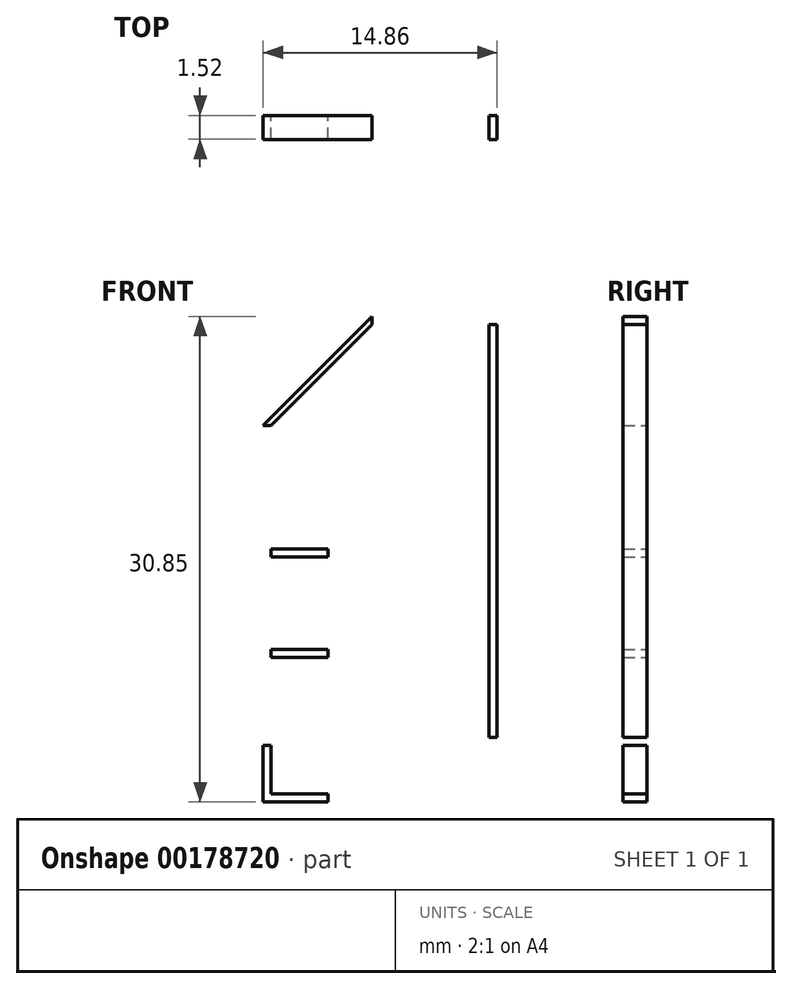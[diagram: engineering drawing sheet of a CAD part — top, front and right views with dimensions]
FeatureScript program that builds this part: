
annotation { "Feature Type Name" : "Feature", "Feature Type Description" : "" }
export const myFeature = defineFeature(function(context is Context, id is Id, definition is map)
    precondition{}
    {
        {
            var Q0;
            Q0=qCreatedBy(makeId("Front.planeOp"),FACE);
            var sketch = newSketch(context, id + "F0", { "sketchPlane" : qUnion([Q0])});
            skLineSegment(sketch, "E0", {"start": v(9.23, -10.4) * mm, "end": v(9.23, 27.78) * mm, "construction": true});
            skLineSegment(sketch, "E1", {"start": v(9.23, -10.4) * mm, "end": v(-1, -10.4) * mm, "construction": true});
            skLineSegment(sketch, "E2", {"start": v(-1, -10.4) * mm, "end": v(-1, -14.01) * mm, "construction": true});
            skLineSegment(sketch, "E3", {"start": v(-1, -14.01) * mm, "end": v(-5.12, -14.01) * mm, "construction": true});
            skLineSegment(sketch, "E4", {"start": v(-5.12, -14.01) * mm, "end": v(-5.12, -13.5) * mm, "construction": true});
            skLineSegment(sketch, "E5", {"start": v(-5.12, -13.5) * mm, "end": v(-15.44, -13.5) * mm, "construction": true});
            skLineSegment(sketch, "E6.bottom", {"start": v(9.23, -9.89) * mm, "end": v(8.73, -9.89) * mm});
            skLineSegment(sketch, "E6.top", {"start": v(9.23, 16.33) * mm, "end": v(8.73, 16.33) * mm});
            skLineSegment(sketch, "E6.left", {"start": v(9.23, -10.4) * mm, "end": v(9.23, 16.33) * mm});
            skLineSegment(sketch, "E6.right", {"start": v(8.73, -9.89) * mm, "end": v(8.73, 16.33) * mm});
            skLineSegment(sketch, "E7.bottom", {"start": v(9.23, -10.4) * mm, "end": v(-5.63, -10.4) * mm});
            skLineSegment(sketch, "E7.top", {"start": v(9.23, -9.89) * mm, "end": v(-5.63, -9.89) * mm});
            skLineSegment(sketch, "E7.left", {"start": v(9.23, -10.4) * mm, "end": v(9.23, -9.89) * mm});
            skLineSegment(sketch, "E7.right", {"start": v(-5.63, -10.4) * mm, "end": v(-5.63, -9.89) * mm});
            skLineSegment(sketch, "E8.bottom", {"start": v(-1, -10.4) * mm, "end": v(-1.52, -10.4) * mm});
            skLineSegment(sketch, "E8.top", {"start": v(-1, -14.01) * mm, "end": v(-1.52, -14.01) * mm});
            skLineSegment(sketch, "E8.left", {"start": v(-1, -10.4) * mm, "end": v(-1, -14.01) * mm});
            skLineSegment(sketch, "E8.right", {"start": v(-1.52, -10.4) * mm, "end": v(-1.52, -14.01) * mm});
            skLineSegment(sketch, "E9.bottom", {"start": v(-1.52, -14.01) * mm, "end": v(-5.12, -14.01) * mm});
            skLineSegment(sketch, "E9.top", {"start": v(-1.52, -13.5) * mm, "end": v(-5.12, -13.5) * mm});
            skLineSegment(sketch, "E9.left", {"start": v(-1.52, -14.01) * mm, "end": v(-1.52, -13.5) * mm});
            skLineSegment(sketch, "E9.right", {"start": v(-5.12, -14.01) * mm, "end": v(-5.12, -13.5) * mm});
            skLineSegment(sketch, "E10.bottom", {"start": v(-5.12, -14.01) * mm, "end": v(-5.63, -14.01) * mm});
            skLineSegment(sketch, "E10.top", {"start": v(-5.12, -10.4) * mm, "end": v(-5.63, -10.4) * mm});
            skLineSegment(sketch, "E10.left", {"start": v(-5.12, -14.01) * mm, "end": v(-5.12, -10.4) * mm});
            skLineSegment(sketch, "E10.right", {"start": v(-5.63, -14.01) * mm, "end": v(-5.63, -10.4) * mm});
            skLineSegment(sketch, "E11.bottom", {"start": v(9.23, 16.33) * mm, "end": v(1.29, 16.33) * mm});
            skLineSegment(sketch, "E11.top", {"start": v(9.23, 16.84) * mm, "end": v(1.29, 16.84) * mm});
            skLineSegment(sketch, "E11.left", {"start": v(9.23, 16.33) * mm, "end": v(9.23, 16.84) * mm});
            skLineSegment(sketch, "E11.right", {"start": v(1.29, 16.33) * mm, "end": v(1.29, 16.84) * mm});
            skLineSegment(sketch, "E12.bottom", {"start": v(-1, -9.89) * mm, "end": v(-1.52, -9.89) * mm});
            skLineSegment(sketch, "E12.top", {"start": v(-1, 14.04) * mm, "end": v(-1.52, 13.53) * mm});
            skLineSegment(sketch, "E12.left", {"start": v(-1, -9.89) * mm, "end": v(-1, 14.04) * mm});
            skLineSegment(sketch, "E12.right", {"start": v(-1.52, -9.89) * mm, "end": v(-1.52, 13.53) * mm});
            skLineSegment(sketch, "E13.bottom", {"start": v(3.13, -9.89) * mm, "end": v(2.62, -9.89) * mm});
            skLineSegment(sketch, "E13.top", {"start": v(3.13, 16.33) * mm, "end": v(2.62, 16.33) * mm});
            skLineSegment(sketch, "E13.left", {"start": v(3.13, -9.89) * mm, "end": v(3.13, 9.44) * mm});
            skLineSegment(sketch, "E13.right", {"start": v(2.62, -9.89) * mm, "end": v(2.62, 9.44) * mm});
            skLineSegment(sketch, "E14.bottom", {"start": v(-5.63, -9.89) * mm, "end": v(-5.12, -9.89) * mm});
            skLineSegment(sketch, "E14.top", {"start": v(-5.63, 9.93) * mm, "end": v(-5.12, 9.93) * mm});
            skLineSegment(sketch, "E14.left", {"start": v(-5.63, -9.89) * mm, "end": v(-5.63, 9.93) * mm});
            skLineSegment(sketch, "E14.right", {"start": v(-5.12, -9.89) * mm, "end": v(-5.12, 9.93) * mm});
            skLineSegment(sketch, "E15", {"start": v(-5.12, 9.93) * mm, "end": v(-1.52, 13.53) * mm, "construction": true});
            skLineSegment(sketch, "E16", {"start": v(1.29, 16.33) * mm, "end": v(-5.12, 9.93) * mm});
            skLineSegment(sketch, "E17.trimOffspring", {"start": v(-1, 14.04) * mm, "end": v(1.29, 16.33) * mm, "construction": true});
            skLineSegment(sketch, "E18.bottom", {"start": v(-1, 9.95) * mm, "end": v(8.73, 9.95) * mm});
            skLineSegment(sketch, "E18.top", {"start": v(-1, 9.44) * mm, "end": v(8.73, 9.44) * mm});
            skLineSegment(sketch, "E18.left", {"start": v(-1, 9.95) * mm, "end": v(-1, 9.44) * mm});
            skLineSegment(sketch, "E18.right", {"start": v(8.73, 9.95) * mm, "end": v(8.73, 9.44) * mm});
            skLineSegment(sketch, "E19.trimOffspring", {"start": v(2.62, 9.95) * mm, "end": v(2.62, 16.33) * mm});
            skLineSegment(sketch, "E20.trimOffspring", {"start": v(3.13, 9.95) * mm, "end": v(3.13, 16.33) * mm});
            skLineSegment(sketch, "E21.bottom", {"start": v(-5.12, -4.82) * mm, "end": v(-1.52, -4.82) * mm});
            skLineSegment(sketch, "E21.top", {"start": v(-5.12, -4.32) * mm, "end": v(-1.52, -4.32) * mm});
            skLineSegment(sketch, "E21.left", {"start": v(-5.12, -4.82) * mm, "end": v(-5.12, -4.32) * mm});
            skLineSegment(sketch, "E21.right", {"start": v(-1.52, -4.82) * mm, "end": v(-1.52, -4.32) * mm});
            skLineSegment(sketch, "E22.bottom", {"start": v(-5.12, 9.93) * mm, "end": v(-1.52, 9.93) * mm});
            skLineSegment(sketch, "E22.top", {"start": v(-5.12, 9.42) * mm, "end": v(-1.52, 9.42) * mm});
            skLineSegment(sketch, "E22.left", {"start": v(-5.12, 9.93) * mm, "end": v(-5.12, 9.42) * mm});
            skLineSegment(sketch, "E22.right", {"start": v(-1.52, 9.93) * mm, "end": v(-1.52, 9.42) * mm});
            skPoint(sketch, "E23.oppositeSnap0", {"position": v(-1, 2.08) * mm});
            skLineSegment(sketch, "E23.bottom", {"start": v(-5.12, 1.57) * mm, "end": v(-1.52, 1.57) * mm});
            skLineSegment(sketch, "E23.top", {"start": v(-5.12, 2.08) * mm, "end": v(-1.52, 2.08) * mm});
            skLineSegment(sketch, "E23.left", {"start": v(-5.12, 1.57) * mm, "end": v(-5.12, 2.08) * mm});
            skLineSegment(sketch, "E23.right", {"start": v(8.73, 1.57) * mm, "end": v(8.73, 2.08) * mm});
            skLineSegment(sketch, "E24.trimOffspring", {"start": v(3.13, 1.57) * mm, "end": v(8.73, 1.57) * mm});
            skLineSegment(sketch, "E25.trimOffspring", {"start": v(3.13, 2.08) * mm, "end": v(8.73, 2.08) * mm});
            skLineSegment(sketch, "E26.trimOffspring", {"start": v(-1, 1.57) * mm, "end": v(2.62, 1.57) * mm});
            skLineSegment(sketch, "E27.trimOffspring", {"start": v(-1, 2.08) * mm, "end": v(2.62, 2.08) * mm});
            skLineSegment(sketch, "E28", {"start": v(1.29, 16.84) * mm, "end": v(-5.63, 9.93) * mm});
            skSolve(sketch);
        }
        {
            var Q0;
            {var subQ7=sQuery(id+"F0.wireOp",EDGE,"E6.left");Q0=makeQuery(id+"F0.imprint","IMPRINT",FACE,{"disambiguationData":[TD([[makeQuery(id+"F0.imprint","IMPRINT",EDGE,{"derivedFrom":subQ7}),1.0]])]});}
            var Q1;
            {var subQ0=sQuery(id+"F0.wireOp",EDGE,"E7.left");Q1=makeQuery(id+"F0.imprint","IMPRINT",FACE,{"disambiguationData":[TD([[makeQuery(id+"F0.imprint","IMPRINT",EDGE,{"derivedFrom":subQ0}),1.0]])]});}
            var Q2;
            {var subQ7=sQuery(id+"F0.wireOp",EDGE,"E13.bottom");Q2=makeQuery(id+"F0.imprint","IMPRINT",FACE,{"disambiguationData":[TD([[makeQuery(id+"F0.imprint","IMPRINT",EDGE,{"derivedFrom":subQ7}),-1.0]])]});}
            var Q3;
            Q3=makeQuery(id+"F0.imprint","IMPRINT",FACE,{"disambiguationData":[TD([[makeQuery(id+"F0.imprint","IMPRINT",EDGE,{"derivedFrom":sQuery(id+"F0.wireOp",EDGE,"E23.right")}),1.0]])]});
            var Q4;
            {var subQ11=sQuery(id+"F0.wireOp",EDGE,"E18.left");Q4=makeQuery(id+"F0.imprint","IMPRINT",FACE,{"disambiguationData":[TD([[makeQuery(id+"F0.imprint","IMPRINT",EDGE,{"derivedFrom":subQ11}),-1.0]])]});}
            var Q5;
            {var subQ0=sQuery(id+"F0.wireOp",EDGE,"E23.bottom");Q5=makeQuery(id+"F0.imprint","IMPRINT",FACE,{"disambiguationData":[TD([[makeQuery(id+"F0.imprint","IMPRINT",EDGE,{"derivedFrom":subQ0}),1.0]])]});}
            var Q6;
            Q6=makeQuery(id+"F0.imprint","IMPRINT",FACE,{"disambiguationData":[TD([[makeQuery(id+"F0.imprint","IMPRINT",EDGE,{"derivedFrom":sQuery(id+"F0.wireOp",EDGE,"E21.bottom")}),1.0]])]});
            var Q7;
            {var subQ1=sQuery(id+"F0.wireOp",EDGE,"E11.right");Q7=makeQuery(id+"F0.imprint","IMPRINT",FACE,{"disambiguationData":[TD([[makeQuery(id+"F0.imprint","IMPRINT",EDGE,{"derivedFrom":subQ1}),1.0]])]});}
            var Q8;
            {var subQ0=sQuery(id+"F0.wireOp",EDGE,"E9.bottom");Q8=makeQuery(id+"F0.imprint","IMPRINT",FACE,{"disambiguationData":[TD([[makeQuery(id+"F0.imprint","IMPRINT",EDGE,{"derivedFrom":subQ0}),-1.0]])]});}
            var Q9;
            Q9=makeQuery(id+"F0.imprint","IMPRINT",FACE,{"disambiguationData":[TD([[makeQuery(id+"F0.imprint","IMPRINT",EDGE,{"derivedFrom":sQuery(id+"F0.wireOp",EDGE,"E8.bottom")}),1.0]])]});
            var Q10;
            {var subQ3=sQuery(id+"F0.wireOp",EDGE,"E10.bottom");Q10=makeQuery(id+"F0.imprint","IMPRINT",FACE,{"disambiguationData":[TD([[makeQuery(id+"F0.imprint","IMPRINT",EDGE,{"derivedFrom":subQ3}),-1.0]])]});}
            var Q11;
            Q11=makeQuery(id+"F0.imprint","IMPRINT",FACE,{"disambiguationData":[TD([[makeQuery(id+"F0.imprint","IMPRINT",EDGE,{"derivedFrom":sQuery(id+"F0.wireOp",EDGE,"E13.top")}),1.0]])]});
            extrude(context, id + "F1", {"entities" : qUnion([Q0, Q1, Q2, Q3, Q4, Q5, Q6, Q7, Q8, Q9, Q10, Q11]), "depth" : 1.52 * mm});
        }
    });
